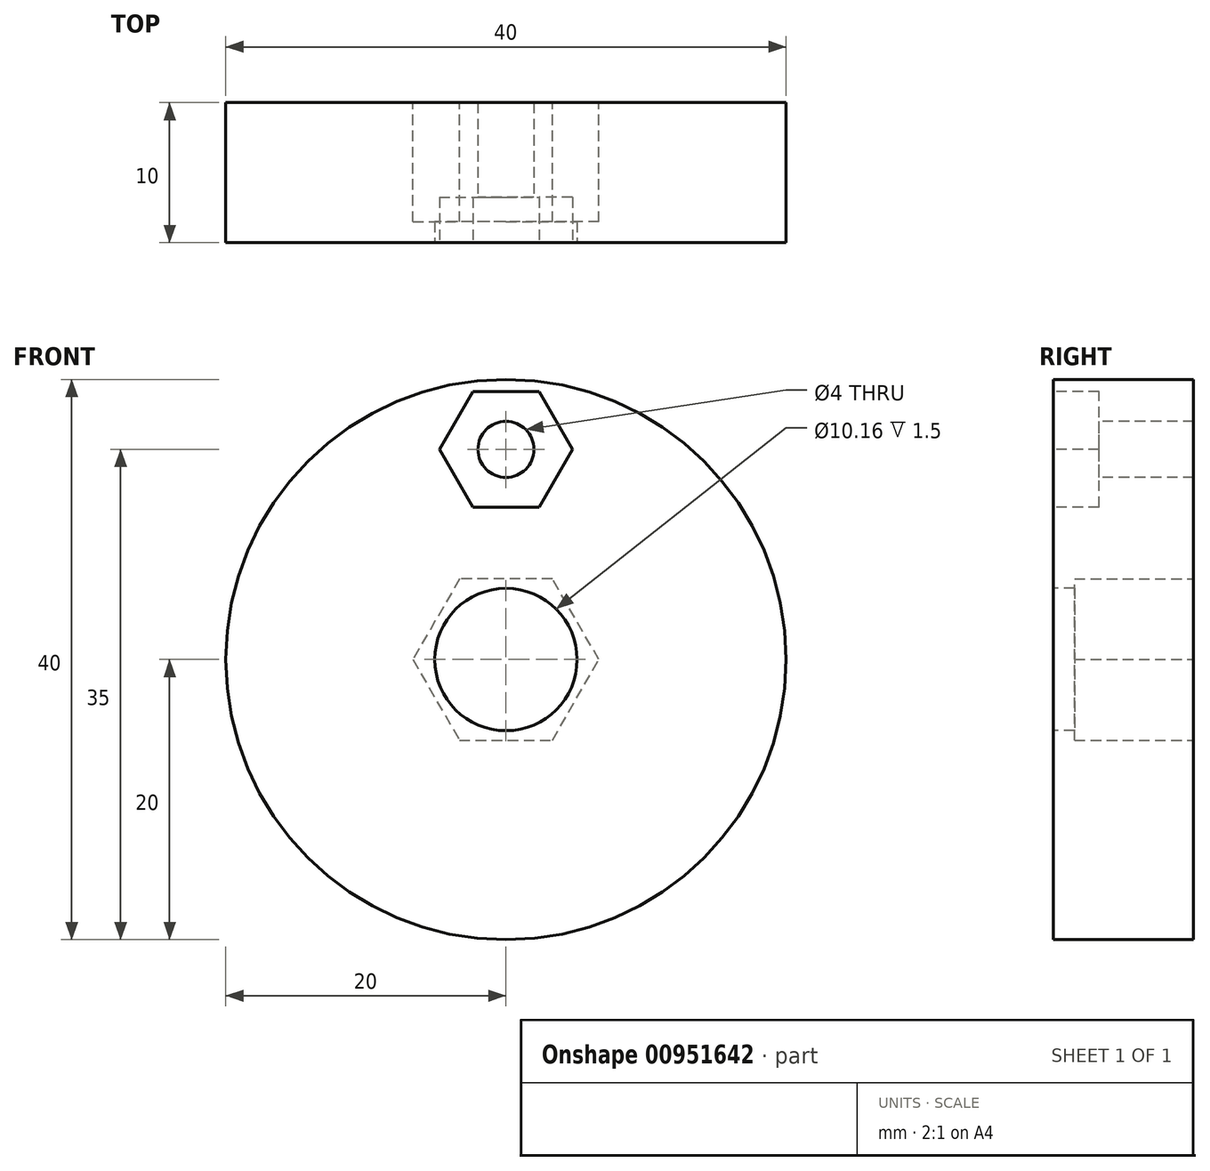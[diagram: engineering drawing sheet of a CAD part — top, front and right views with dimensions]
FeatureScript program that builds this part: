
annotation { "Feature Type Name" : "Feature", "Feature Type Description" : "" }
export const myFeature = defineFeature(function(context is Context, id is Id, definition is map)
    precondition{}
    {
        {
            var Q0;
            Q0=qCreatedBy(makeId("Front.planeOp"),FACE);
            var sketch = newSketch(context, id + "F0", { "sketchPlane" : qUnion([Q0])});
            skCircle(sketch, "E0", {"center": v(0, 0) * mm, "radius": 20 * mm});
            skSolve(sketch);
        }
        {
            var Q0;
            Q0 = qSketchRegion(id + "F0", true);
            extrude(context, id + "F1", {"entities" : qUnion([Q0]), "depth" : 10 * mm, "offsetDistance" : 25 * mm});
        }
        {
            var Q0;
            Q0=makeQuery(id+"F1.opExtrude","CAP_FACE",FACE,{"disambiguationData":[OSD([sQuery(id+"F0.wireOp",EDGE,"E0")])],"isStart":true});
            var sketch = newSketch(context, id + "F2", { "sketchPlane" : qUnion([Q0])});
            skCircle(sketch, "E1.cCircle", {"center": v(0, 0) * mm, "radius": 5.75 * mm, "construction": true});
            skLineSegment(sketch, "E1.0", {"start": v(-3.32, 5.75) * mm, "end": v(3.32, 5.75) * mm});
            skLineSegment(sketch, "E1.1", {"start": v(3.32, 5.75) * mm, "end": v(6.64, 0) * mm});
            skLineSegment(sketch, "E1.2", {"start": v(6.64, 0) * mm, "end": v(3.32, -5.75) * mm});
            skLineSegment(sketch, "E1.3", {"start": v(3.32, -5.75) * mm, "end": v(-3.32, -5.75) * mm});
            skLineSegment(sketch, "E1.4", {"start": v(-3.32, -5.75) * mm, "end": v(-6.64, 0) * mm});
            skLineSegment(sketch, "E1.5", {"start": v(-6.64, 0) * mm, "end": v(-3.32, 5.75) * mm});
            skPoint(sketch, "E1.0.midPoint", {"position": v(0, 5.75) * mm});
            skSolve(sketch);
        }
        {
            var Q0;
            Q0 = qSketchRegion(id + "F2", true);
            extrude(context, id + "F3", {"entities" : qUnion([Q0]), "operationType" : NewBodyOperationType.REMOVE, "oppositeDirection" : true, "depth" : 8.5 * mm, "offsetDistance" : 25 * mm});
        }
        {
            var Q0;
            Q0=makeQuery(id+"F1.opExtrude","CAP_FACE",FACE,{"disambiguationData":[OSD([sQuery(id+"F0.wireOp",EDGE,"E0")])],"isStart":false});
            var sketch = newSketch(context, id + "F4", { "sketchPlane" : qUnion([Q0])});
            skCircle(sketch, "E2", {"center": v(0, 15) * mm, "radius": 2 * mm});
            skSolve(sketch);
        }
        {
            var Q0;
            Q0 = qSketchRegion(id + "F4", true);
            extrude(context, id + "F5", {"entities" : qUnion([Q0]), "operationType" : NewBodyOperationType.REMOVE, "endBound" : BoundingType.THROUGH_ALL, "oppositeDirection" : true, "depth" : 25 * mm, "offsetDistance" : 25 * mm});
        }
        {
            var Q0;
            Q0=makeQuery(id+"F1.opExtrude","CAP_FACE",FACE,{"disambiguationData":[OSD([sQuery(id+"F0.wireOp",EDGE,"E0")])],"isStart":false});
            var sketch = newSketch(context, id + "F6", { "sketchPlane" : qUnion([Q0])});
            skCircle(sketch, "E3.cCircle", {"center": v(0, 15) * mm, "radius": 4.11 * mm, "construction": true});
            skLineSegment(sketch, "E3.0", {"start": v(-2.38, 19.11) * mm, "end": v(2.37, 19.11) * mm});
            skLineSegment(sketch, "E3.1", {"start": v(2.37, 19.11) * mm, "end": v(4.75, 15) * mm});
            skLineSegment(sketch, "E3.2", {"start": v(4.75, 15) * mm, "end": v(2.38, 10.89) * mm});
            skLineSegment(sketch, "E3.3", {"start": v(2.38, 10.89) * mm, "end": v(-2.37, 10.89) * mm});
            skLineSegment(sketch, "E3.4", {"start": v(-2.37, 10.89) * mm, "end": v(-4.75, 15) * mm});
            skLineSegment(sketch, "E3.5", {"start": v(-4.75, 15) * mm, "end": v(-2.38, 19.11) * mm});
            skPoint(sketch, "E3.0.midPoint", {"position": v(0, 19.11) * mm});
            skSolve(sketch);
        }
        {
            var Q0;
            Q0 = qSketchRegion(id + "F6", true);
            extrude(context, id + "F7", {"entities" : qUnion([Q0]), "operationType" : NewBodyOperationType.REMOVE, "oppositeDirection" : true, "depth" : 3.25 * mm, "offsetDistance" : 25 * mm});
        }
        {
            var Q0;
            Q0=makeQuery(id+"F1.opExtrude","CAP_FACE",FACE,{"disambiguationData":[OSD([sQuery(id+"F0.wireOp",EDGE,"E0")])],"isStart":false});
            var sketch = newSketch(context, id + "F8", { "sketchPlane" : qUnion([Q0])});
            skCircle(sketch, "E4", {"center": v(0, 0) * mm, "radius": 5.08 * mm});
            skSolve(sketch);
        }
        {
            var Q0;
            Q0 = qSketchRegion(id + "F8", true);
            extrude(context, id + "F9", {"entities" : qUnion([Q0]), "operationType" : NewBodyOperationType.REMOVE, "endBound" : BoundingType.THROUGH_ALL, "oppositeDirection" : true, "depth" : 25 * mm, "offsetDistance" : 25 * mm});
        }
    });
